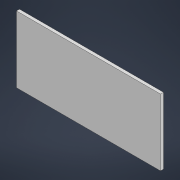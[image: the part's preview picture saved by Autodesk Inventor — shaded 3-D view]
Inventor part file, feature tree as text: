
AUTODESK INVENTOR PART (.ipt)
format: ipt  version: 2022 (Build 260153000, 153)  size: 83,968 bytes
history: native  units: mm
features: other x1, extrude x1, sketch x1
ambient origin geometry x8: Origin, YZ Plane, XZ Plane, XY Plane, X Axis, Y Axis, Z Axis, Center Point
bodies: Body1 (feature_tree)
feature tree (3):
  other  "Твердое тело1"
  extrude  "Выдавливание1"  Depth=576.0mm
  sketch  "Эскиз1"
